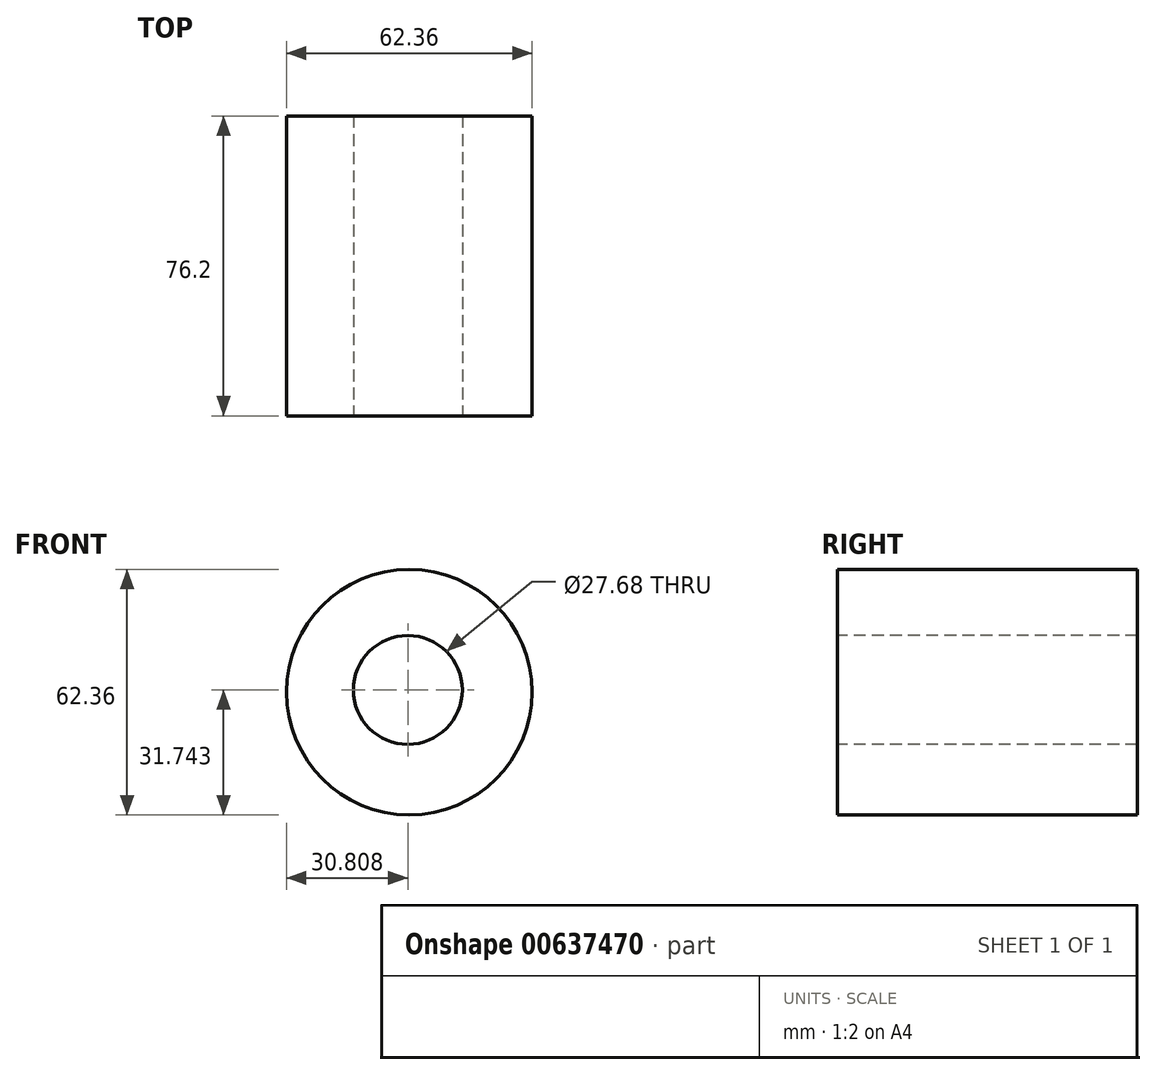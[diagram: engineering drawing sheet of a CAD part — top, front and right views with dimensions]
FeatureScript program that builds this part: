
annotation { "Feature Type Name" : "Feature", "Feature Type Description" : "" }
export const myFeature = defineFeature(function(context is Context, id is Id, definition is map)
    precondition{}
    {
        {
            var Q0;
            Q0=qCreatedBy(makeId("Front.planeOp"),FACE);
            var sketch = newSketch(context, id + "F0", { "sketchPlane" : qUnion([Q0])});
            skCircle(sketch, "E0", {"center": v(-33.8, 40.6) * mm, "radius": 31.18 * mm});
            skSolve(sketch);
        }
        {
            var Q0;
            Q0 = qSketchRegion(id + "F0", true);
            extrude(context, id + "F1", {"entities" : qUnion([Q0]), "depth" : 76.2 * mm, "offsetDistance" : 25.4 * mm});
        }
        {
            var Q0;
            Q0=makeQuery(id+"F1.opExtrude","CAP_FACE",FACE,{"disambiguationData":[OSD([sQuery(id+"F0.wireOp",EDGE,"E0")])],"isStart":false});
            var sketch = newSketch(context, id + "F2", { "sketchPlane" : qUnion([Q0])});
            skSolve(sketch);
        }
        {
            var Q0;
            Q0=makeQuery(id+"F2.imprint","IMPRINT",FACE,{"disambiguationData":[TD([[makeQuery(id+"F2.imprint","IMPRINT",EDGE,{"derivedFrom":makeQuery(id+"F1.opExtrude","CAP_EDGE",EDGE,{"disambiguationData":[OSD([sQuery(id+"F0.wireOp",EDGE,"E0")])],"isStart":false})}),1.0]])]});
            var sketch = newSketch(context, id + "F3", { "sketchPlane" : qUnion([Q0])});
            skCircle(sketch, "E1", {"center": v(-34.18, 41.16) * mm, "radius": 13.84 * mm});
            skSolve(sketch);
        }
        {
            var Q0;
            Q0=makeQuery(id+"F3.imprint","IMPRINT",FACE,{"disambiguationData":[TD([[makeQuery(id+"F3.imprint","IMPRINT",EDGE,{"derivedFrom":sQuery(id+"F3.wireOp",EDGE,"E1")}),1.0]])]});
            extrude(context, id + "F4", {"entities" : qUnion([Q0]), "operationType" : NewBodyOperationType.REMOVE, "oppositeDirection" : true, "depth" : 254 * mm, "offsetDistance" : 25.4 * mm});
        }
    });
